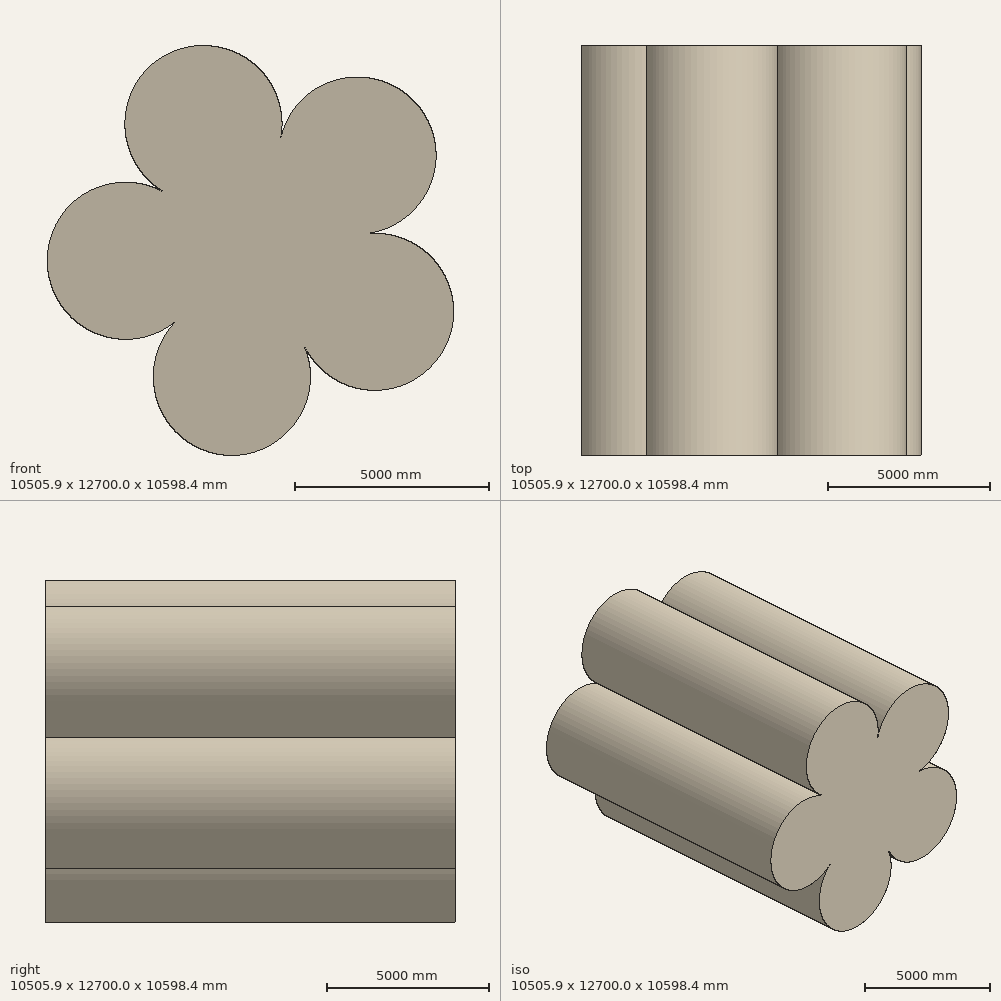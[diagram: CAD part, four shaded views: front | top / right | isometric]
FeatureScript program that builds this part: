
annotation { "Feature Type Name" : "Feature", "Feature Type Description" : "" }
export const myFeature = defineFeature(function(context is Context, id is Id, definition is map)
    precondition{}
    {
        {
            var Q0;
            Q0=qCreatedBy(makeId("Front.planeOp"),FACE);
            var sketch = newSketch(context, id + "F0", { "sketchPlane" : qUnion([Q0])});
            skCircle(sketch, "E0", {"center": v(1760.2, 1015.25) * mm, "radius": 2032 * mm});
            skCircle(sketch, "E1", {"center": v(-4227.07, -1703.64) * mm, "radius": 2032 * mm});
            skCircle(sketch, "E2", {"center": v(-2221.13, 1830.8) * mm, "radius": 2032 * mm});
            skCircle(sketch, "E3", {"center": v(2214.85, -3023.24) * mm, "radius": 2032 * mm});
            skCircle(sketch, "E4", {"center": v(-1485.48, -4703.6) * mm, "radius": 2032 * mm});
            skLineSegment(sketch, "E5", {"start": v(-2221.13, 1830.8) * mm, "end": v(-4227.07, -1703.64) * mm, "construction": true});
            skLineSegment(sketch, "E6", {"start": v(-4227.07, -1703.64) * mm, "end": v(-1485.48, -4703.6) * mm, "construction": true});
            skLineSegment(sketch, "E7", {"start": v(-1485.48, -4703.6) * mm, "end": v(2214.85, -3023.24) * mm, "construction": true});
            skLineSegment(sketch, "E8", {"start": v(2214.85, -3023.24) * mm, "end": v(1760.2, 1015.25) * mm, "construction": true});
            skLineSegment(sketch, "E9", {"start": v(-2221.13, 1830.8) * mm, "end": v(1760.2, 1015.25) * mm, "construction": true});
            skSolve(sketch);
        }
        {
            var Q0;
            Q0 = qSketchRegion(id + "F0", true);
            extrude(context, id + "F1", {"entities" : qUnion([Q0]), "depth" : 12700 * mm, "offsetDistance" : 25.4 * mm});
        }
    });
